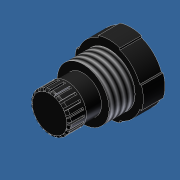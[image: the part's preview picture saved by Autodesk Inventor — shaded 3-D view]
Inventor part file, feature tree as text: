
AUTODESK INVENTOR PART (.ipt)
format: ipt  version: 2011 (Build 150239000, 239)  size: 294,912 bytes
history: native  units: in
note: dims shown in document units (in); Inventor stores cm internally (conversion verified against a paired STEP export)
features: extrude x6, sketch x6, thread x1, pattern_circular x1, fillet x1
ambient origin geometry x8: Origin, YZ Plane, XZ Plane, XY Plane, X Axis, Y Axis, Z Axis, Center Point
bodies: Solid1 (feature_tree)
feature tree (15):
  extrude  "Extrusion1"  Depth=0.5in TaperAngle=0.0deg
  extrude  "Extrusion2"  Depth=0.25in
  extrude  "Extrusion3"  Depth=0.25in
  thread  "Thread1"  [1 undecoded]
  extrude  "Extrusion4"  Depth=0.6in TaperAngle=0.0deg
  extrude  "Extrusion5"  Depth=0.85in
  extrude  "Extrusion6"  Depth=0.9in
  pattern_circular  "Circular Pattern1"  [2 undecoded]
  fillet  "Fillet1"  Radius=0.05in
  sketch  "Sketch1"  dims[d0=1.5in d1=0.5in d2=0.0in]
  sketch  "Sketch2"  dims[d3=0.5in d4=0.25in]
  sketch  "Sketch3"  dims[d5=0.5in d6=0.25in d7=0.5in d8=0.0in]
  sketch  "Sketch4"  dims[d9=1.2in d10=0.6in d11=0.0in]
  sketch  "Sketch5"  dims[d12=1.0in d13=0.0in d14=0.85in]
  sketch  "Sketch6"  dims[d15=0.375in d16=0.0in d17=0.9in d18=0.4in d19=0.0in d20=0.05in d21=0.025in d22=0.05in d23=0.35in d24=0.0in d25=7.874in d26=360.0deg d28=0.05in]
note: 3 required parameter values undecoded (feature->parameter linkage not recoverable at this tier; creation-order binding heuristic only, values carry confidence <= 0.55)
